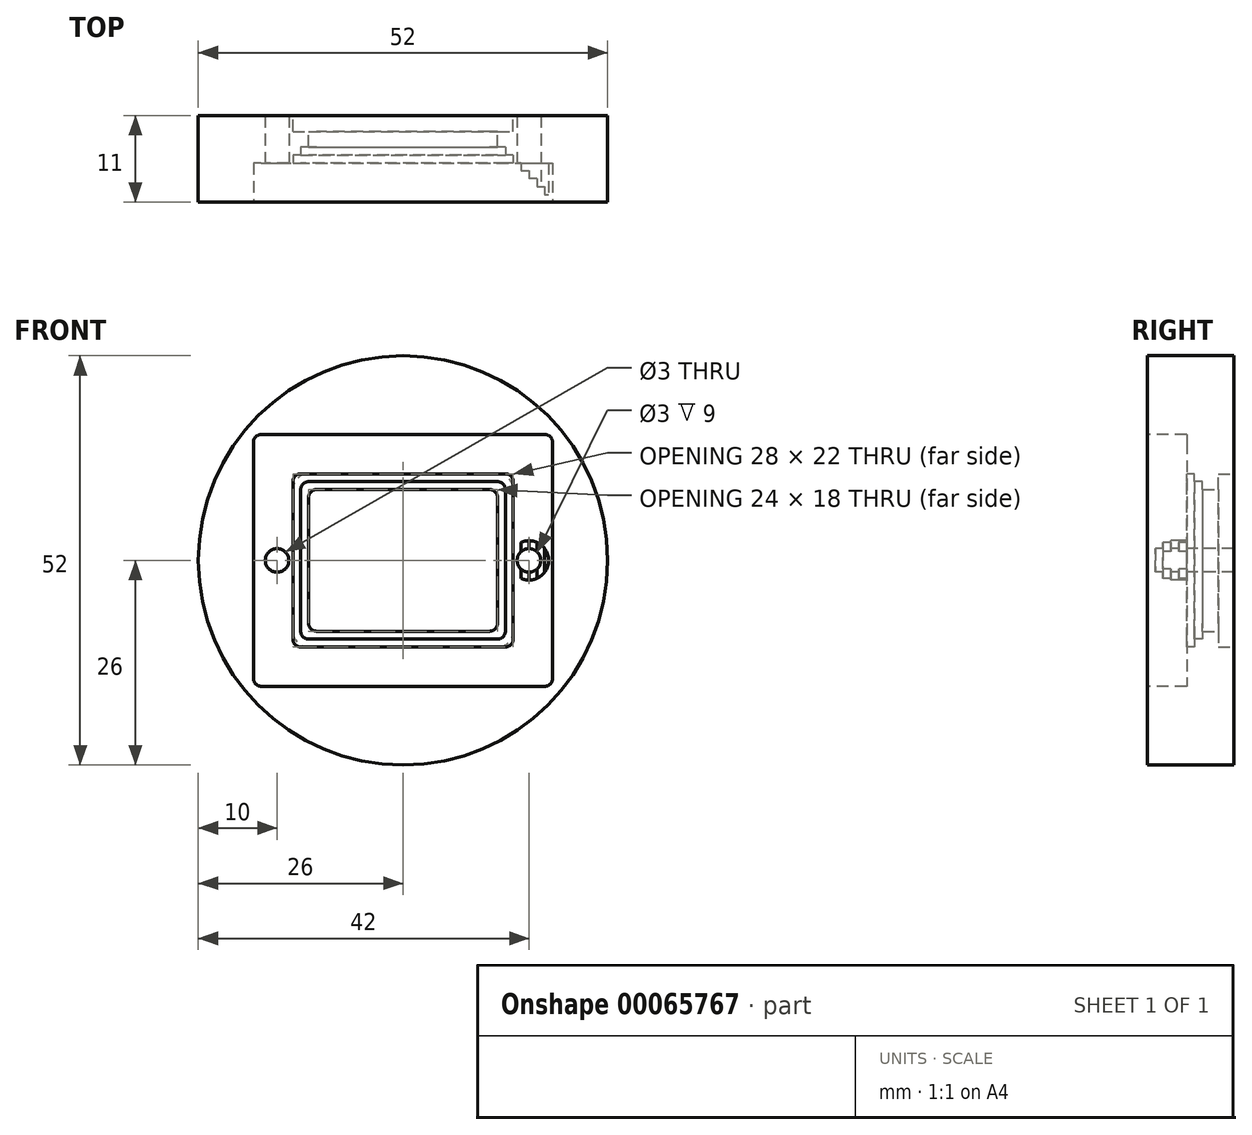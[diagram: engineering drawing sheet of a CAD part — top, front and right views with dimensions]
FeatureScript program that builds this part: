
annotation { "Feature Type Name" : "Feature", "Feature Type Description" : "" }
export const myFeature = defineFeature(function(context is Context, id is Id, definition is map)
    precondition{}
    {
        {
            var Q0;
            Q0=qCreatedBy(makeId("Front.planeOp"),FACE);
            var sketch = newSketch(context, id + "F0", { "sketchPlane" : qUnion([Q0])});
            skCircle(sketch, "E0", {"center": v(0, 0) * mm, "radius": 26 * mm});
            skLineSegment(sketch, "E1.bottom", {"start": v(-12, 9) * mm, "end": v(12, 9) * mm});
            skLineSegment(sketch, "E1.top", {"start": v(-12, -9) * mm, "end": v(12, -9) * mm});
            skLineSegment(sketch, "E1.left", {"start": v(-12, 9) * mm, "end": v(-12, -9) * mm});
            skLineSegment(sketch, "E1.right", {"start": v(12, 9) * mm, "end": v(12, -9) * mm});
            skLineSegment(sketch, "E2", {"start": v(-12, 9) * mm, "end": v(12, -9) * mm, "construction": true});
            skLineSegment(sketch, "E3", {"start": v(-12, -9) * mm, "end": v(12, 9) * mm, "construction": true});
            skSolve(sketch);
        }
        {
            var Q0;
            Q0=qSketchRegion(id+"F0",true);
            extrude(context, id + "F1", {"entities" : qUnion([Q0]), "depth" : 11 * mm});
        }
        {
            var Q0;
            Q0=makeQuery(id+"F1.opExtrude","CAP_FACE",FACE,{"disambiguationData":[OSD([sQuery(id+"F0.wireOp",EDGE,"E0"),sQuery(id+"F0.wireOp",EDGE,"E1.bottom"),sQuery(id+"F0.wireOp",EDGE,"E1.top"),sQuery(id+"F0.wireOp",EDGE,"E1.left"),sQuery(id+"F0.wireOp",EDGE,"E1.right")])],"isStart":true});
            var sketch = newSketch(context, id + "F2", { "sketchPlane" : qUnion([Q0])});
            skLineSegment(sketch, "E4.bottom", {"start": v(12, 11) * mm, "end": v(-12, 11) * mm});
            skLineSegment(sketch, "E4.top", {"start": v(12, -11) * mm, "end": v(-12, -11) * mm});
            skLineSegment(sketch, "E4.left", {"start": v(14, 9) * mm, "end": v(14, -9) * mm});
            skLineSegment(sketch, "E4.right", {"start": v(-14, 9) * mm, "end": v(-14, -9) * mm});
            skPoint(sketch, "E5.visualSharp", {"position": v(-14, 11) * mm});
            skArc(sketch, "E5.filletArc", {"start": v(-12, 11) * mm, "mid": v(-13.41, 10.41) * mm, "end": v(-14, 9) * mm});
            skPoint(sketch, "E6.visualSharp", {"position": v(14, 11) * mm});
            skArc(sketch, "E6.filletArc", {"start": v(14, 9) * mm, "mid": v(13.41, 10.41) * mm, "end": v(12, 11) * mm});
            skPoint(sketch, "E7.visualSharp", {"position": v(14, -11) * mm});
            skArc(sketch, "E7.filletArc", {"start": v(12, -11) * mm, "mid": v(13.41, -10.41) * mm, "end": v(14, -9) * mm});
            skPoint(sketch, "E8.visualSharp", {"position": v(-14, -11) * mm});
            skArc(sketch, "E8.filletArc", {"start": v(-14, -9) * mm, "mid": v(-13.41, -10.41) * mm, "end": v(-12, -11) * mm});
            skSolve(sketch);
        }
        {
            var Q0;
            Q0=qSketchRegion(id+"F2",true);
            extrude(context, id + "F3", {"entities" : qUnion([Q0]), "operationType" : NewBodyOperationType.REMOVE, "oppositeDirection" : true, "depth" : 2 * mm});
        }
        {
            var Q0;
            Q0=makeQuery(id+"F1.opExtrude","CAP_FACE",FACE,{"disambiguationData":[OSD([sQuery(id+"F0.wireOp",EDGE,"E0"),sQuery(id+"F0.wireOp",EDGE,"E1.bottom"),sQuery(id+"F0.wireOp",EDGE,"E1.top"),sQuery(id+"F0.wireOp",EDGE,"E1.left"),sQuery(id+"F0.wireOp",EDGE,"E1.right")])],"isStart":false});
            var sketch = newSketch(context, id + "F4", { "sketchPlane" : qUnion([Q0])});
            skLineSegment(sketch, "E9.bottom", {"start": v(-13, 10) * mm, "end": v(13, 10) * mm});
            skLineSegment(sketch, "E9.top", {"start": v(-13, -10) * mm, "end": v(13, -10) * mm});
            skLineSegment(sketch, "E9.left", {"start": v(-13, 10) * mm, "end": v(-13, -10) * mm});
            skLineSegment(sketch, "E9.right", {"start": v(13, 10) * mm, "end": v(13, -10) * mm});
            skSolve(sketch);
        }
        {
            var Q0;
            Q0=qSketchRegion(id+"F4",true);
            extrude(context, id + "F5", {"entities" : qUnion([Q0]), "operationType" : NewBodyOperationType.REMOVE, "oppositeDirection" : true, "depth" : 7 * mm});
        }
        {
            var Q0;
            Q0=makeQuery(id+"F1.opExtrude","CAP_FACE",FACE,{"disambiguationData":[OSD([sQuery(id+"F0.wireOp",EDGE,"E0"),sQuery(id+"F0.wireOp",EDGE,"E1.bottom"),sQuery(id+"F0.wireOp",EDGE,"E1.top"),sQuery(id+"F0.wireOp",EDGE,"E1.left"),sQuery(id+"F0.wireOp",EDGE,"E1.right")])],"isStart":false});
            var sketch = newSketch(context, id + "F6", { "sketchPlane" : qUnion([Q0])});
            skLineSegment(sketch, "E10.bottom", {"start": v(-14, 11) * mm, "end": v(14, 11) * mm});
            skLineSegment(sketch, "E10.top", {"start": v(-14, -11) * mm, "end": v(14, -11) * mm});
            skLineSegment(sketch, "E10.left", {"start": v(-14, 11) * mm, "end": v(-14, -11) * mm});
            skLineSegment(sketch, "E10.right", {"start": v(14, 11) * mm, "end": v(14, -11) * mm});
            skSolve(sketch);
        }
        {
            var Q0;
            Q0=qSketchRegion(id+"F6",true);
            extrude(context, id + "F7", {"entities" : qUnion([Q0]), "operationType" : NewBodyOperationType.REMOVE, "oppositeDirection" : true, "depth" : 6 * mm});
        }
        {
            var Q0;
            Q0=makeQuery(id+"F1.opExtrude","CAP_FACE",FACE,{"disambiguationData":[OSD([sQuery(id+"F0.wireOp",EDGE,"E0"),sQuery(id+"F0.wireOp",EDGE,"E1.bottom"),sQuery(id+"F0.wireOp",EDGE,"E1.top"),sQuery(id+"F0.wireOp",EDGE,"E1.left"),sQuery(id+"F0.wireOp",EDGE,"E1.right")])],"isStart":false});
            var sketch = newSketch(context, id + "F8", { "sketchPlane" : qUnion([Q0])});
            skLineSegment(sketch, "E11.bottom", {"start": v(-15, 12) * mm, "end": v(15, 12) * mm});
            skLineSegment(sketch, "E11.top", {"start": v(-15, -12) * mm, "end": v(15, -12) * mm});
            skLineSegment(sketch, "E11.left", {"start": v(-15, 12) * mm, "end": v(-15, -12) * mm});
            skLineSegment(sketch, "E11.right", {"start": v(15, 12) * mm, "end": v(15, -12) * mm});
            skSolve(sketch);
        }
        {
            var Q0;
            Q0=qSketchRegion(id+"F8",true);
            extrude(context, id + "F9", {"entities" : qUnion([Q0]), "operationType" : NewBodyOperationType.REMOVE, "oppositeDirection" : true, "depth" : 5 * mm});
        }
        {
            var Q0;
            Q0=makeQuery(id+"F1.opExtrude","CAP_FACE",FACE,{"disambiguationData":[OSD([sQuery(id+"F0.wireOp",EDGE,"E0"),sQuery(id+"F0.wireOp",EDGE,"E1.bottom"),sQuery(id+"F0.wireOp",EDGE,"E1.top"),sQuery(id+"F0.wireOp",EDGE,"E1.left"),sQuery(id+"F0.wireOp",EDGE,"E1.right")])],"isStart":false});
            var sketch = newSketch(context, id + "F10", { "sketchPlane" : qUnion([Q0])});
            skLineSegment(sketch, "E12.bottom", {"start": v(-16, 13) * mm, "end": v(16, 13) * mm});
            skLineSegment(sketch, "E12.top", {"start": v(-16, -13) * mm, "end": v(16, -13) * mm});
            skLineSegment(sketch, "E12.left", {"start": v(-16, 13) * mm, "end": v(-16, -13) * mm});
            skLineSegment(sketch, "E12.right", {"start": v(16, 13) * mm, "end": v(16, -13) * mm});
            skSolve(sketch);
        }
        {
            var Q0;
            Q0=qSketchRegion(id+"F10",true);
            extrude(context, id + "F11", {"entities" : qUnion([Q0]), "operationType" : NewBodyOperationType.REMOVE, "oppositeDirection" : true, "depth" : 4 * mm});
        }
        {
            var Q0;
            Q0=qSketchRegion(id+"F10",true);
            extrude(context, id + "F12", {"entities" : qUnion([Q0]), "operationType" : NewBodyOperationType.REMOVE, "oppositeDirection" : true, "depth" : 4 * mm});
        }
        {
            var Q0;
            Q0=makeQuery(id+"F1.opExtrude","CAP_FACE",FACE,{"disambiguationData":[OSD([sQuery(id+"F0.wireOp",EDGE,"E0"),sQuery(id+"F0.wireOp",EDGE,"E1.bottom"),sQuery(id+"F0.wireOp",EDGE,"E1.top"),sQuery(id+"F0.wireOp",EDGE,"E1.left"),sQuery(id+"F0.wireOp",EDGE,"E1.right")])],"isStart":false});
            var sketch = newSketch(context, id + "F13", { "sketchPlane" : qUnion([Q0])});
            skLineSegment(sketch, "E13.bottom", {"start": v(-17, 14) * mm, "end": v(17, 14) * mm});
            skLineSegment(sketch, "E13.top", {"start": v(-17, -14) * mm, "end": v(17, -14) * mm});
            skLineSegment(sketch, "E13.left", {"start": v(-17, 14) * mm, "end": v(-17, -14) * mm});
            skLineSegment(sketch, "E13.right", {"start": v(17, 14) * mm, "end": v(17, -14) * mm});
            skSolve(sketch);
        }
        {
            var Q0;
            Q0=qSketchRegion(id+"F13",true);
            extrude(context, id + "F14", {"entities" : qUnion([Q0]), "operationType" : NewBodyOperationType.REMOVE, "oppositeDirection" : true, "depth" : 3 * mm});
        }
        {
            var Q0;
            Q0=makeQuery(id+"F1.opExtrude","CAP_FACE",FACE,{"disambiguationData":[OSD([sQuery(id+"F0.wireOp",EDGE,"E0"),sQuery(id+"F0.wireOp",EDGE,"E1.bottom"),sQuery(id+"F0.wireOp",EDGE,"E1.top"),sQuery(id+"F0.wireOp",EDGE,"E1.left"),sQuery(id+"F0.wireOp",EDGE,"E1.right")])],"isStart":false});
            var sketch = newSketch(context, id + "F15", { "sketchPlane" : qUnion([Q0])});
            skLineSegment(sketch, "E14.bottom", {"start": v(-18, 15) * mm, "end": v(18, 15) * mm});
            skLineSegment(sketch, "E14.top", {"start": v(-18, -15) * mm, "end": v(18, -15) * mm});
            skLineSegment(sketch, "E14.left", {"start": v(-18, 15) * mm, "end": v(-18, -15) * mm});
            skLineSegment(sketch, "E14.right", {"start": v(18, 15) * mm, "end": v(18, -15) * mm});
            skSolve(sketch);
        }
        {
            var Q0;
            Q0=makeQuery(id+"F15.imprint","IMPRINT",FACE,{"disambiguationData":[TD([[makeQuery(id+"F15.imprint","IMPRINT",EDGE,{"derivedFrom":sQuery(id+"F15.wireOp",EDGE,"E14.bottom")}),-1.0]])]});
            extrude(context, id + "F16", {"entities" : qUnion([Q0]), "operationType" : NewBodyOperationType.REMOVE, "oppositeDirection" : true, "depth" : 2 * mm});
        }
        {
            var Q0;
            Q0=makeQuery(id+"F1.opExtrude","CAP_FACE",FACE,{"disambiguationData":[OSD([sQuery(id+"F0.wireOp",EDGE,"E0"),sQuery(id+"F0.wireOp",EDGE,"E1.bottom"),sQuery(id+"F0.wireOp",EDGE,"E1.top"),sQuery(id+"F0.wireOp",EDGE,"E1.left"),sQuery(id+"F0.wireOp",EDGE,"E1.right")])],"isStart":false});
            var sketch = newSketch(context, id + "F17", { "sketchPlane" : qUnion([Q0])});
            skLineSegment(sketch, "E15.bottom", {"start": v(-19, 16) * mm, "end": v(19, 16) * mm});
            skLineSegment(sketch, "E15.top", {"start": v(-19, -16) * mm, "end": v(19, -16) * mm});
            skLineSegment(sketch, "E15.left", {"start": v(-19, 16) * mm, "end": v(-19, -16) * mm});
            skLineSegment(sketch, "E15.right", {"start": v(19, 16) * mm, "end": v(19, -16) * mm});
            skSolve(sketch);
        }
        {
            var Q0;
            Q0=makeQuery(id+"F17.imprint","IMPRINT",FACE,{"disambiguationData":[TD([[makeQuery(id+"F17.imprint","IMPRINT",EDGE,{"derivedFrom":sQuery(id+"F17.wireOp",EDGE,"E15.bottom")}),-1.0]])]});
            extrude(context, id + "F18", {"entities" : qUnion([Q0]), "operationType" : NewBodyOperationType.REMOVE, "oppositeDirection" : true, "depth" : 1 * mm});
        }
        {
            var Q0;
            Q0=makeQuery(id+"F9.boolean.opBoolean","COPY",EDGE,{"derivedFrom":makeQuery(id+"F9.opExtrude","SWEPT_EDGE",EDGE,{"disambiguationData":[OSD([sQuery(id+"F8.wireOp",EDGE,"E11.top"),sQuery(id+"F8.wireOp",EDGE,"E11.right")])]})});
            var Q1;
            Q1=makeQuery(id+"F5.boolean.opBoolean","COPY",EDGE,{"derivedFrom":makeQuery(id+"F5.opExtrude","SWEPT_EDGE",EDGE,{"disambiguationData":[OSD([sQuery(id+"F4.wireOp",EDGE,"E9.top"),sQuery(id+"F4.wireOp",EDGE,"E9.right")])]})});
            var Q2;
            Q2=makeQuery(id+"F7.boolean.opBoolean","COPY",EDGE,{"derivedFrom":makeQuery(id+"F7.opExtrude","SWEPT_EDGE",EDGE,{"disambiguationData":[OSD([sQuery(id+"F6.wireOp",EDGE,"E10.top"),sQuery(id+"F6.wireOp",EDGE,"E10.right")])]})});
            var Q3;
            Q3=makeQuery(id+"F1.opExtrude","SWEPT_EDGE",EDGE,{"disambiguationData":[OSD([sQuery(id+"F0.wireOp",EDGE,"E1.top"),sQuery(id+"F0.wireOp",EDGE,"E1.right")])]});
            var Q4;
            Q4=makeQuery(id+"F9.boolean.opBoolean","COPY",EDGE,{"derivedFrom":makeQuery(id+"F9.opExtrude","SWEPT_EDGE",EDGE,{"disambiguationData":[OSD([sQuery(id+"F8.wireOp",EDGE,"E11.top"),sQuery(id+"F8.wireOp",EDGE,"E11.left")])]})});
            var Q5;
            Q5=makeQuery(id+"F7.boolean.opBoolean","COPY",EDGE,{"derivedFrom":makeQuery(id+"F7.opExtrude","SWEPT_EDGE",EDGE,{"disambiguationData":[OSD([sQuery(id+"F6.wireOp",EDGE,"E10.top"),sQuery(id+"F6.wireOp",EDGE,"E10.left")])]})});
            var Q6;
            Q6=makeQuery(id+"F5.boolean.opBoolean","COPY",EDGE,{"derivedFrom":makeQuery(id+"F5.opExtrude","SWEPT_EDGE",EDGE,{"disambiguationData":[OSD([sQuery(id+"F4.wireOp",EDGE,"E9.top"),sQuery(id+"F4.wireOp",EDGE,"E9.left")])]})});
            var Q7;
            Q7=makeQuery(id+"F1.opExtrude","SWEPT_EDGE",EDGE,{"disambiguationData":[OSD([sQuery(id+"F0.wireOp",EDGE,"E1.top"),sQuery(id+"F0.wireOp",EDGE,"E1.left")])]});
            var Q8;
            Q8=makeQuery(id+"F1.opExtrude","SWEPT_EDGE",EDGE,{"disambiguationData":[OSD([sQuery(id+"F0.wireOp",EDGE,"E1.bottom"),sQuery(id+"F0.wireOp",EDGE,"E1.left")])]});
            var Q9;
            Q9=makeQuery(id+"F5.boolean.opBoolean","COPY",EDGE,{"derivedFrom":makeQuery(id+"F5.opExtrude","SWEPT_EDGE",EDGE,{"disambiguationData":[OSD([sQuery(id+"F4.wireOp",EDGE,"E9.bottom"),sQuery(id+"F4.wireOp",EDGE,"E9.left")])]})});
            var Q10;
            Q10=makeQuery(id+"F7.boolean.opBoolean","COPY",EDGE,{"derivedFrom":makeQuery(id+"F7.opExtrude","SWEPT_EDGE",EDGE,{"disambiguationData":[OSD([sQuery(id+"F6.wireOp",EDGE,"E10.bottom"),sQuery(id+"F6.wireOp",EDGE,"E10.left")])]})});
            var Q11;
            Q11=makeQuery(id+"F9.boolean.opBoolean","COPY",EDGE,{"derivedFrom":makeQuery(id+"F9.opExtrude","SWEPT_EDGE",EDGE,{"disambiguationData":[OSD([sQuery(id+"F8.wireOp",EDGE,"E11.bottom"),sQuery(id+"F8.wireOp",EDGE,"E11.left")])]})});
            var Q12;
            Q12=makeQuery(id+"F9.boolean.opBoolean","COPY",EDGE,{"derivedFrom":makeQuery(id+"F9.opExtrude","SWEPT_EDGE",EDGE,{"disambiguationData":[OSD([sQuery(id+"F8.wireOp",EDGE,"E11.bottom"),sQuery(id+"F8.wireOp",EDGE,"E11.right")])]})});
            var Q13;
            Q13=makeQuery(id+"F7.boolean.opBoolean","COPY",EDGE,{"derivedFrom":makeQuery(id+"F7.opExtrude","SWEPT_EDGE",EDGE,{"disambiguationData":[OSD([sQuery(id+"F6.wireOp",EDGE,"E10.bottom"),sQuery(id+"F6.wireOp",EDGE,"E10.right")])]})});
            var Q14;
            Q14=makeQuery(id+"F1.opExtrude","SWEPT_EDGE",EDGE,{"disambiguationData":[OSD([sQuery(id+"F0.wireOp",EDGE,"E1.bottom"),sQuery(id+"F0.wireOp",EDGE,"E1.right")])]});
            var Q15;
            Q15=makeQuery(id+"F5.boolean.opBoolean","COPY",EDGE,{"derivedFrom":makeQuery(id+"F5.opExtrude","SWEPT_EDGE",EDGE,{"disambiguationData":[OSD([sQuery(id+"F4.wireOp",EDGE,"E9.bottom"),sQuery(id+"F4.wireOp",EDGE,"E9.right")])]})});
            var Q16;
            Q16=makeQuery(id+"F11.boolean.opBoolean","COPY",EDGE,{"derivedFrom":makeQuery(id+"F11.opExtrude","SWEPT_EDGE",EDGE,{"disambiguationData":[OSD([sQuery(id+"F10.wireOp",EDGE,"E12.top"),sQuery(id+"F10.wireOp",EDGE,"E12.right")])]})});
            var Q17;
            Q17=makeQuery(id+"F14.boolean.opBoolean","COPY",EDGE,{"derivedFrom":makeQuery(id+"F14.opExtrude","SWEPT_EDGE",EDGE,{"disambiguationData":[OSD([sQuery(id+"F13.wireOp",EDGE,"E13.top"),sQuery(id+"F13.wireOp",EDGE,"E13.right")])]})});
            var Q18;
            Q18=makeQuery(id+"F16.boolean.opBoolean","COPY",EDGE,{"derivedFrom":makeQuery(id+"F16.opExtrude","SWEPT_EDGE",EDGE,{"disambiguationData":[OSD([sQuery(id+"F15.wireOp",EDGE,"E14.top"),sQuery(id+"F15.wireOp",EDGE,"E14.right")])]})});
            var Q19;
            Q19=makeQuery(id+"F18.boolean.opBoolean","COPY",EDGE,{"derivedFrom":makeQuery(id+"F18.opExtrude","SWEPT_EDGE",EDGE,{"disambiguationData":[OSD([sQuery(id+"F17.wireOp",EDGE,"E15.top"),sQuery(id+"F17.wireOp",EDGE,"E15.right")])]})});
            var Q20;
            Q20=makeQuery(id+"F11.boolean.opBoolean","COPY",EDGE,{"derivedFrom":makeQuery(id+"F11.opExtrude","SWEPT_EDGE",EDGE,{"disambiguationData":[OSD([sQuery(id+"F10.wireOp",EDGE,"E12.top"),sQuery(id+"F10.wireOp",EDGE,"E12.left")])]})});
            var Q21;
            Q21=makeQuery(id+"F14.boolean.opBoolean","COPY",EDGE,{"derivedFrom":makeQuery(id+"F14.opExtrude","SWEPT_EDGE",EDGE,{"disambiguationData":[OSD([sQuery(id+"F13.wireOp",EDGE,"E13.top"),sQuery(id+"F13.wireOp",EDGE,"E13.left")])]})});
            var Q22;
            Q22=makeQuery(id+"F16.boolean.opBoolean","COPY",EDGE,{"derivedFrom":makeQuery(id+"F16.opExtrude","SWEPT_EDGE",EDGE,{"disambiguationData":[OSD([sQuery(id+"F15.wireOp",EDGE,"E14.top"),sQuery(id+"F15.wireOp",EDGE,"E14.left")])]})});
            var Q23;
            Q23=makeQuery(id+"F18.boolean.opBoolean","COPY",EDGE,{"derivedFrom":makeQuery(id+"F18.opExtrude","SWEPT_EDGE",EDGE,{"disambiguationData":[OSD([sQuery(id+"F17.wireOp",EDGE,"E15.top"),sQuery(id+"F17.wireOp",EDGE,"E15.left")])]})});
            var Q24;
            Q24=makeQuery(id+"F11.boolean.opBoolean","COPY",EDGE,{"derivedFrom":makeQuery(id+"F11.opExtrude","SWEPT_EDGE",EDGE,{"disambiguationData":[OSD([sQuery(id+"F10.wireOp",EDGE,"E12.bottom"),sQuery(id+"F10.wireOp",EDGE,"E12.left")])]})});
            var Q25;
            Q25=makeQuery(id+"F14.boolean.opBoolean","COPY",EDGE,{"derivedFrom":makeQuery(id+"F14.opExtrude","SWEPT_EDGE",EDGE,{"disambiguationData":[OSD([sQuery(id+"F13.wireOp",EDGE,"E13.bottom"),sQuery(id+"F13.wireOp",EDGE,"E13.left")])]})});
            var Q26;
            Q26=makeQuery(id+"F16.boolean.opBoolean","COPY",EDGE,{"derivedFrom":makeQuery(id+"F16.opExtrude","SWEPT_EDGE",EDGE,{"disambiguationData":[OSD([sQuery(id+"F15.wireOp",EDGE,"E14.bottom"),sQuery(id+"F15.wireOp",EDGE,"E14.left")])]})});
            var Q27;
            Q27=makeQuery(id+"F18.boolean.opBoolean","COPY",EDGE,{"derivedFrom":makeQuery(id+"F18.opExtrude","SWEPT_EDGE",EDGE,{"disambiguationData":[OSD([sQuery(id+"F17.wireOp",EDGE,"E15.bottom"),sQuery(id+"F17.wireOp",EDGE,"E15.left")])]})});
            var Q28;
            Q28=makeQuery(id+"F18.boolean.opBoolean","COPY",EDGE,{"derivedFrom":makeQuery(id+"F18.opExtrude","SWEPT_EDGE",EDGE,{"disambiguationData":[OSD([sQuery(id+"F17.wireOp",EDGE,"E15.bottom"),sQuery(id+"F17.wireOp",EDGE,"E15.right")])]})});
            var Q29;
            Q29=makeQuery(id+"F16.boolean.opBoolean","COPY",EDGE,{"derivedFrom":makeQuery(id+"F16.opExtrude","SWEPT_EDGE",EDGE,{"disambiguationData":[OSD([sQuery(id+"F15.wireOp",EDGE,"E14.bottom"),sQuery(id+"F15.wireOp",EDGE,"E14.right")])]})});
            var Q30;
            Q30=makeQuery(id+"F11.boolean.opBoolean","COPY",EDGE,{"derivedFrom":makeQuery(id+"F11.opExtrude","SWEPT_EDGE",EDGE,{"disambiguationData":[OSD([sQuery(id+"F10.wireOp",EDGE,"E12.bottom"),sQuery(id+"F10.wireOp",EDGE,"E12.right")])]})});
            var Q31;
            Q31=makeQuery(id+"F14.boolean.opBoolean","COPY",EDGE,{"derivedFrom":makeQuery(id+"F14.opExtrude","SWEPT_EDGE",EDGE,{"disambiguationData":[OSD([sQuery(id+"F13.wireOp",EDGE,"E13.bottom"),sQuery(id+"F13.wireOp",EDGE,"E13.right")])]})});
            fillet(context, id + "F19", {"entities" : qUnion([Q0, Q1, Q2, Q3, Q4, Q5, Q6, Q7, Q8, Q9, Q10, Q11, Q12, Q13, Q14, Q15, Q16, Q17, Q18, Q19, Q20, Q21, Q22, Q23, Q24, Q25, Q26, Q27, Q28, Q29, Q30, Q31]), "radius" : 1 * mm, "tangentPropagation" : true, "allowEdgeOverflow" : false});
        }
        {
            var Q0;
            Q0=makeQuery(id+"F1.opExtrude","CAP_FACE",FACE,{"disambiguationData":[OSD([sQuery(id+"F0.wireOp",EDGE,"E0"),sQuery(id+"F0.wireOp",EDGE,"E1.bottom"),sQuery(id+"F0.wireOp",EDGE,"E1.top"),sQuery(id+"F0.wireOp",EDGE,"E1.left"),sQuery(id+"F0.wireOp",EDGE,"E1.right")])],"isStart":false});
            var sketch = newSketch(context, id + "F20", { "sketchPlane" : qUnion([Q0])});
            skCircle(sketch, "E16", {"center": v(-16, 0) * mm, "radius": 1.5 * mm});
            skCircle(sketch, "E17.MirrorC", {"center": v(16, 0) * mm, "radius": 1.5 * mm});
            skSolve(sketch);
        }
        {
            var Q0;
            Q0=qSketchRegion(id+"F20",true);
            extrude(context, id + "F21", {"entities" : qUnion([Q0]), "operationType" : NewBodyOperationType.REMOVE, "oppositeDirection" : true, "depth" : 25 * mm});
        }
        {
            var Q0;
            Q0=makeQuery(id+"F1.opExtrude","CAP_FACE",FACE,{"disambiguationData":[OSD([sQuery(id+"F0.wireOp",EDGE,"E0"),sQuery(id+"F0.wireOp",EDGE,"E1.bottom"),sQuery(id+"F0.wireOp",EDGE,"E1.top"),sQuery(id+"F0.wireOp",EDGE,"E1.left"),sQuery(id+"F0.wireOp",EDGE,"E1.right")])],"isStart":false});
            var sketch = newSketch(context, id + "F22", { "sketchPlane" : qUnion([Q0])});
            skCircle(sketch, "E18", {"center": v(-16, 0) * mm, "radius": 2.5 * mm});
            skCircle(sketch, "E19.MirrorC", {"center": v(16, 0) * mm, "radius": 2.5 * mm});
            skSolve(sketch);
        }
        {
            var Q0;
            Q0=makeQuery(id+"F22.imprint","IMPRINT",FACE,{"disambiguationData":[TD([[makeQuery(id+"F22.imprint","IMPRINT",EDGE,{"derivedFrom":sQuery(id+"F22.wireOp",EDGE,"E18")}),1.0]])]});
            var Q1;
            Q1=makeQuery(id+"F22.imprint","IMPRINT",FACE,{"disambiguationData":[TD([[makeQuery(id+"F22.imprint","IMPRINT",EDGE,{"derivedFrom":sQuery(id+"F22.wireOp",EDGE,"E19.MirrorC")}),-1.0]])]});
            extrude(context, id + "F23", {"entities" : qUnion([Q0, Q1]), "operationType" : NewBodyOperationType.REMOVE, "oppositeDirection" : true, "depth" : 5 * mm});
        }
    });
